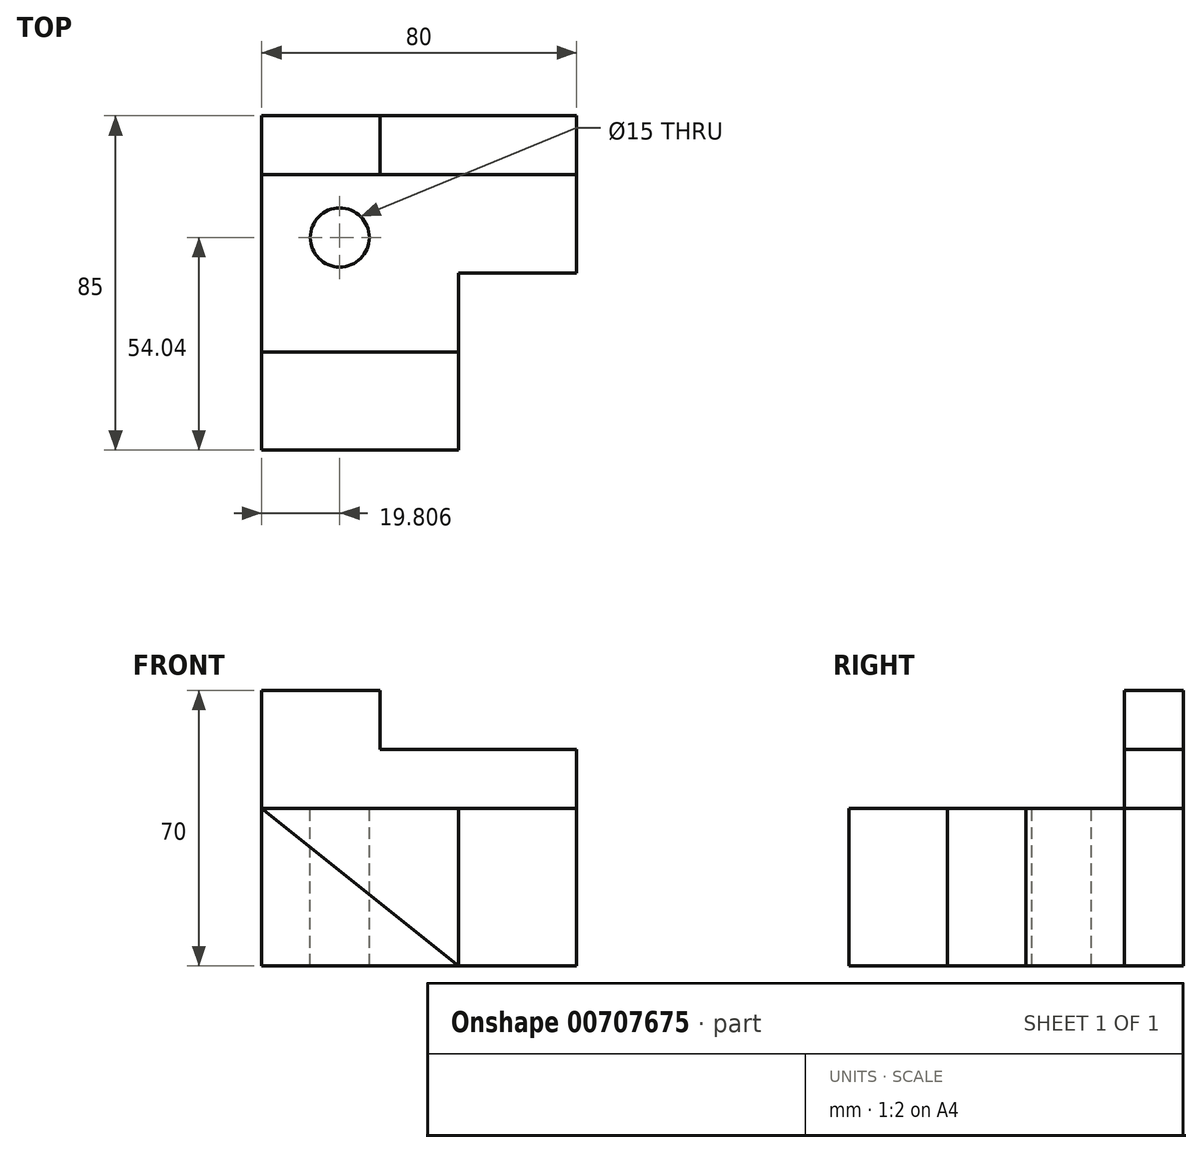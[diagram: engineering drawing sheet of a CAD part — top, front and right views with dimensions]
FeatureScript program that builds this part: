
annotation { "Feature Type Name" : "Feature", "Feature Type Description" : "" }
export const myFeature = defineFeature(function(context is Context, id is Id, definition is map)
    precondition{}
    {
        {
            var Q0;
            Q0=qCreatedBy(makeId("Front.planeOp"),FACE);
            var sketch = newSketch(context, id + "F0", { "sketchPlane" : qUnion([Q0])});
            skLineSegment(sketch, "E0", {"start": v(0, 0) * mm, "end": v(0, 40) * mm});
            skLineSegment(sketch, "E1", {"start": v(0, 0) * mm, "end": v(50, 0) * mm});
            skLineSegment(sketch, "E2", {"start": v(50, 0) * mm, "end": v(0, 40) * mm});
            skSolve(sketch);
        }
        {
            var Q0;
            Q0=makeQuery(id+"F0.imprint","IMPRINT",FACE,{"disambiguationData":[TD([[makeQuery(id+"F0.imprint","IMPRINT",EDGE,{"derivedFrom":sQuery(id+"F0.wireOp",EDGE,"E0")}),-1.0]])]});
            extrude(context, id + "F1", {"entities" : qUnion([Q0]), "oppositeDirection" : true, "depth" : 25 * mm, "offsetDistance" : 25 * mm});
        }
        {
            var Q0;
            Q0=qCreatedBy(makeId("Top.planeOp"),FACE);
            var sketch = newSketch(context, id + "F2", { "sketchPlane" : qUnion([Q0])});
            skLineSegment(sketch, "E3", {"start": v(0, 25) * mm, "end": v(0, 70) * mm});
            skLineSegment(sketch, "E4", {"start": v(0, 70) * mm, "end": v(80, 70) * mm});
            skLineSegment(sketch, "E5", {"start": v(80, 70) * mm, "end": v(80, 45) * mm});
            skLineSegment(sketch, "E6", {"start": v(0, 25) * mm, "end": v(50, 25) * mm});
            skLineSegment(sketch, "E7", {"start": v(80, 45) * mm, "end": v(50, 45) * mm});
            skLineSegment(sketch, "E8", {"start": v(50, 45) * mm, "end": v(50, 25) * mm});
            skSolve(sketch);
        }
        {
            var Q0;
            Q0=makeQuery(id+"F2.imprint","IMPRINT",FACE,{"disambiguationData":[TD([[makeQuery(id+"F2.imprint","IMPRINT",EDGE,{"derivedFrom":sQuery(id+"F2.wireOp",EDGE,"E3")}),-1.0]])]});
            extrude(context, id + "F3", {"entities" : qUnion([Q0]), "operationType" : NewBodyOperationType.ADD, "depth" : 40 * mm, "offsetDistance" : 25 * mm});
        }
        {
            var Q0;
            Q0=makeQuery(id+"F3.opExtrude","SWEPT_FACE",FACE,{"disambiguationData":[OSD([sQuery(id+"F2.wireOp",EDGE,"E4")])]});
            var sketch = newSketch(context, id + "F4", { "sketchPlane" : qUnion([Q0])});
            skLineSegment(sketch, "E9", {"start": v(0, 0) * mm, "end": v(0, 70) * mm});
            skLineSegment(sketch, "E10", {"start": v(0, 70) * mm, "end": v(-30, 70) * mm});
            skLineSegment(sketch, "E11", {"start": v(-30, 70) * mm, "end": v(-30, 55) * mm});
            skLineSegment(sketch, "E12", {"start": v(-30, 55) * mm, "end": v(-80, 55) * mm});
            skLineSegment(sketch, "E13", {"start": v(-80, 55) * mm, "end": v(-80, 40) * mm});
            skSolve(sketch);
        }
        {
            var Q0;
            {var subQ0=sQuery(id+"F4.wireOp",EDGE,"E10");Q0=makeQuery(id+"F4.imprint","IMPRINT",FACE,{"disambiguationData":[TD([[makeQuery(id+"F4.imprint","IMPRINT",EDGE,{"derivedFrom":subQ0}),1.0]])]});}
            extrude(context, id + "F5", {"entities" : qUnion([Q0]), "depth" : 15 * mm, "offsetDistance" : 25 * mm});
        }
        {
            var Q0;
            Q0=makeQuery(id+"F5.opExtrude","SWEPT_FACE",FACE,{"disambiguationData":[OSD([sQuery(id+"F2.wireOp",EDGE,"E4")])]});
            extrude(context, id + "F6", {"entities" : qUnion([Q0]), "depth" : 40 * mm, "offsetDistance" : 25 * mm});
        }
        {
            var Q0;
            Q0=makeQuery(id+"F3.opExtrude","CAP_FACE",FACE,{"disambiguationData":[OSD([sQuery(id+"F2.wireOp",EDGE,"E3"),sQuery(id+"F2.wireOp",EDGE,"E4"),sQuery(id+"F2.wireOp",EDGE,"E5"),sQuery(id+"F2.wireOp",EDGE,"E6"),sQuery(id+"F2.wireOp",EDGE,"E7"),sQuery(id+"F2.wireOp",EDGE,"E8")])],"isStart":false});
            var sketch = newSketch(context, id + "F7", { "sketchPlane" : qUnion([Q0])});
            skCircle(sketch, "E14", {"center": v(19.8, 54.04) * mm, "radius": 7.5 * mm});
            skSolve(sketch);
        }
        {
            var Q0;
            Q0=makeQuery(id+"F7.imprint","IMPRINT",FACE,{"disambiguationData":[TD([[makeQuery(id+"F7.imprint","IMPRINT",EDGE,{"derivedFrom":sQuery(id+"F7.wireOp",EDGE,"E14")}),1.0]])]});
            extrude(context, id + "F8", {"entities" : qUnion([Q0]), "operationType" : NewBodyOperationType.REMOVE, "endBound" : BoundingType.UP_TO_NEXT, "oppositeDirection" : true, "depth" : 25 * mm, "offsetDistance" : 25 * mm});
        }
    });
